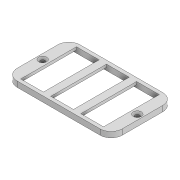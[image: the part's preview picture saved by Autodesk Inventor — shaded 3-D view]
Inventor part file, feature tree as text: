
AUTODESK INVENTOR PART (.ipt)
format: ipt  version: 2021 (Build 250183000, 183)  size: 140,288 bytes
history: native  units: mm
features: sketch x3, extrude x2, hole x1, fillet x1, chamfer x1
ambient origin geometry x8: Origin, YZ Plane, XZ Plane, XY Plane, X Axis, Y Axis, Z Axis, Center Point
bodies: Volumenkörper1 (feature_tree)
feature tree (8):
  extrude  "Extrusion1"  Depth=34.0mm
  extrude  "Extrusion2"  Depth=12.3mm
  hole  "Bohrung1"  [1 undecoded]
  fillet  "Rundung1"  Radius=12.3mm
  chamfer  "Fase1"  Distance=4.0mm
  sketch  "Skizze1"  dims[d0=56.9mm d1=34.0mm]
  sketch  "Skizze2"  dims[d2=3.0mm d3=0.0mm d4=12.3mm]
  sketch  "Skizze3"  dims[d5=30.2mm d6=12.3mm d7=30.2mm d8=12.3mm d9=30.2mm d10=4.0mm d11=4.0mm d12=6.0mm d13=6.0mm d14=3.0mm d15=0.0mm d16=51.3mm d17=20.0mm d18=2.4mm d19=6.0mm d20=4.4mm d21=2.0mm d22=90.0deg d23=8.0mm d24=20.594885mm d25=6.0mm d26=1.5mm d27=2.0mm d28=45.0deg]
note: 1 required parameter value undecoded (feature->parameter linkage not recoverable at this tier; creation-order binding heuristic only, values carry confidence <= 0.55)
